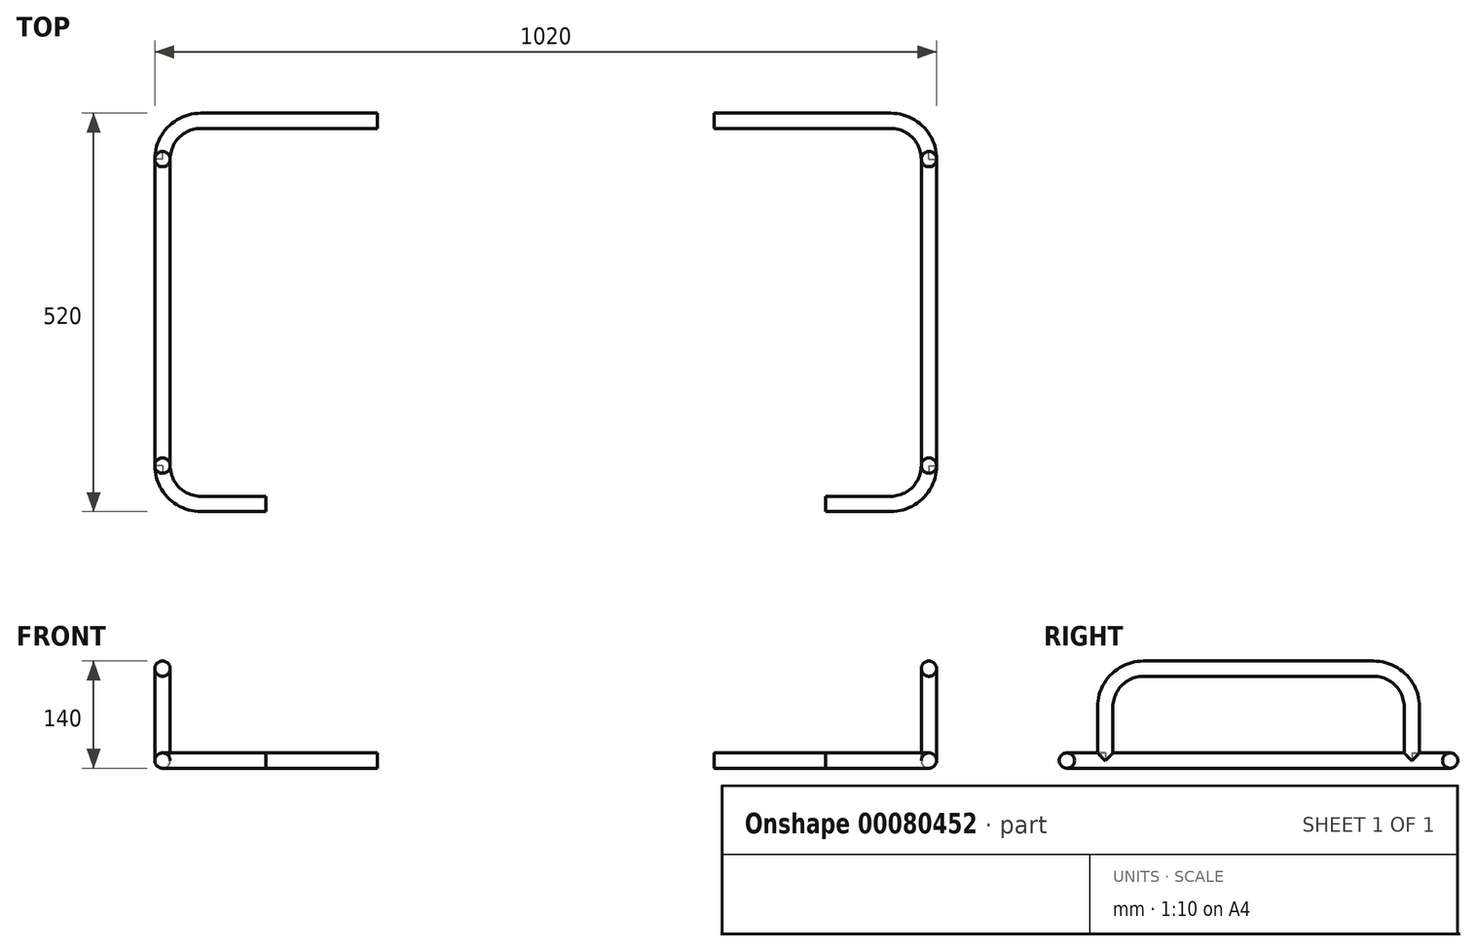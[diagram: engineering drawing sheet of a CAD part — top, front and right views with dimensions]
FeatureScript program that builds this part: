
annotation { "Feature Type Name" : "Feature", "Feature Type Description" : "" }
export const myFeature = defineFeature(function(context is Context, id is Id, definition is map)
    precondition{}
    {
        {
            var Q0;
            Q0=qCreatedBy(makeId("Top.planeOp"),FACE);
            var sketch = newSketch(context, id + "F0", { "sketchPlane" : qUnion([Q0])});
            skLineSegment(sketch, "E0", {"start": v(0, 0) * mm, "end": v(55, 0) * mm});
            skLineSegment(sketch, "E1", {"start": v(105, 50) * mm, "end": v(105, 450) * mm});
            skLineSegment(sketch, "E2", {"start": v(55, 500) * mm, "end": v(-145, 500) * mm});
            skLineSegment(sketch, "E3", {"start": v(-395, 732.64) * mm, "end": v(-395, -307.47) * mm, "construction": true});
            skPoint(sketch, "E4.visualSharp", {"position": v(105, 0) * mm});
            skArc(sketch, "E4.filletArc", {"start": v(55, 0) * mm, "mid": v(90.36, 14.64) * mm, "end": v(105, 50) * mm});
            skPoint(sketch, "E5.visualSharp", {"position": v(105, 500) * mm});
            skArc(sketch, "E5.filletArc", {"start": v(105, 450) * mm, "mid": v(90.36, 485.36) * mm, "end": v(55, 500) * mm});
            skSolve(sketch);
        }
        {
            var Q0;
            Q0=qCreatedBy(makeId("Right.planeOp"),FACE);
            var sketch = newSketch(context, id + "F1", { "sketchPlane" : qUnion([Q0])});
            skCircle(sketch, "E6", {"center": v(0, 0) * mm, "radius": 10 * mm});
            skSolve(sketch);
        }
        {
            var Q0;
            Q0=makeQuery(id+"F1.imprint","IMPRINT",FACE,{"disambiguationData":[TD([[makeQuery(id+"F1.imprint","IMPRINT",EDGE,{"derivedFrom":sQuery(id+"F1.wireOp",EDGE,"E6")}),1.0]])]});
            var Q1;
            Q1=sQuery(id+"F0.wireOp",EDGE,"E0");
            var Q2;
            Q2=sQuery(id+"F0.wireOp",EDGE,"E4.filletArc");
            var Q3;
            Q3=sQuery(id+"F0.wireOp",EDGE,"E1");
            var Q4;
            Q4=sQuery(id+"F0.wireOp",EDGE,"E5.filletArc");
            var Q5;
            Q5=sQuery(id+"F0.wireOp",EDGE,"E2");
            sweep(context, id + "F2", {"profiles" : qUnion([Q0]), "path" : qUnion([Q1, Q2, Q3, Q4, Q5])});
        }
        {
            var Q0;
            Q0=makeQuery(id+"F2.opSweep","CAP_FACE",FACE,{"disambiguationData":[OSD([sQuery(id+"F0.wireOp",VERTEX,"E0.start"),sQuery(id+"F1.wireOp",EDGE,"E6")])],"isStart":true});
            var Q1;
            Q1=makeQuery(id+"F2.opSweep","CAP_FACE",FACE,{"disambiguationData":[OSD([sQuery(id+"F0.wireOp",VERTEX,"E2.end"),sQuery(id+"F1.wireOp",EDGE,"E6")])],"isStart":false});
            extrude(context, id + "F3", {"entities" : qUnion([Q0, Q1]), "operationType" : NewBodyOperationType.ADD, "depth" : 30 * mm});
        }
        {
            var Q0;
            Q0=qCreatedBy(makeId("Right.planeOp"),FACE);
            var Q1;
            Q1=sQuery(id+"F0.wireOp",VERTEX,"E4.filletArc.end");
            cPlane(context, id + "F4", {"entities" : qUnion([Q0, Q1]), "cplaneType" : CPlaneType.PLANE_POINT, "offset" : 150 * mm, "width" : 150 * mm, "height" : 150 * mm});
        }
        {
            var Q0;
            Q0=qCreatedBy(id+"F4.planeOp",FACE);
            var sketch = newSketch(context, id + "F5", { "sketchPlane" : qUnion([Q0])});
            skPoint(sketch, "E7.0", {"position": v(50, 0) * mm});
            skPoint(sketch, "E7.1", {"position": v(450, 0) * mm});
            skLineSegment(sketch, "E8", {"start": v(50, 0) * mm, "end": v(50, 70) * mm});
            skLineSegment(sketch, "E9", {"start": v(100, 120) * mm, "end": v(400, 120) * mm});
            skLineSegment(sketch, "E10", {"start": v(450, 70) * mm, "end": v(450, 0) * mm});
            skPoint(sketch, "E11.visualSharp", {"position": v(50, 120) * mm});
            skArc(sketch, "E11.filletArc", {"start": v(100, 120) * mm, "mid": v(64.64, 105.36) * mm, "end": v(50, 70) * mm});
            skPoint(sketch, "E12.visualSharp", {"position": v(450, 120) * mm});
            skArc(sketch, "E12.filletArc", {"start": v(450, 70) * mm, "mid": v(435.36, 105.36) * mm, "end": v(400, 120) * mm});
            skSolve(sketch);
        }
        {
            var Q0;
            Q0=sQuery(id+"F5.wireOp",VERTEX,"E8.end");
            var Q1;
            Q1=sQuery(id+"F5.wireOp",EDGE,"E8");
            cPlane(context, id + "F6", {"entities" : qUnion([Q0, Q1]), "cplaneType" : CPlaneType.LINE_POINT, "offset" : 150 * mm, "width" : 150 * mm, "height" : 150 * mm});
        }
        {
            var Q0;
            Q0=qCreatedBy(id+"F6.planeOp",FACE);
            var sketch = newSketch(context, id + "F7", { "sketchPlane" : qUnion([Q0])});
            skPoint(sketch, "E13.0", {"position": v(105, 50) * mm});
            skCircle(sketch, "E14", {"center": v(105, 50) * mm, "radius": 10 * mm});
            skSolve(sketch);
        }
        {
            var Q0;
            Q0=makeQuery(id+"F7.imprint","IMPRINT",FACE,{"disambiguationData":[TD([[makeQuery(id+"F7.imprint","IMPRINT",EDGE,{"derivedFrom":sQuery(id+"F7.wireOp",EDGE,"E14")}),1.0]])]});
            var Q1;
            Q1=sQuery(id+"F5.wireOp",EDGE,"E11.filletArc");
            var Q2;
            Q2=sQuery(id+"F5.wireOp",EDGE,"E9");
            var Q3;
            Q3=sQuery(id+"F5.wireOp",EDGE,"E12.filletArc");
            sweep(context, id + "F8", {"profiles" : qUnion([Q0]), "path" : qUnion([Q1, Q2, Q3])});
        }
        {
            var Q0;
            Q0=makeQuery(id+"F8.opSweep","CAP_FACE",FACE,{"disambiguationData":[OSD([sQuery(id+"F5.wireOp",VERTEX,"E11.filletArc.end"),sQuery(id+"F7.wireOp",EDGE,"E14")])],"isStart":true});
            var Q1;
            Q1=makeQuery(id+"F8.opSweep","CAP_FACE",FACE,{"disambiguationData":[OSD([sQuery(id+"F5.wireOp",VERTEX,"E12.filletArc.start"),sQuery(id+"F7.wireOp",EDGE,"E14")])],"isStart":false});
            var Q2;
            Q2=makeQuery(id+"F2.opSweep","SWEPT_FACE",FACE,{"disambiguationData":[OSD([sQuery(id+"F0.wireOp",EDGE,"E1"),sQuery(id+"F1.wireOp",EDGE,"E6")])]});
            extrude(context, id + "F9", {"entities" : qUnion([Q0, Q1]), "operationType" : NewBodyOperationType.ADD, "endBound" : BoundingType.UP_TO_SURFACE, "endBoundEntityFace" : qUnion([Q2]), "depth" : 25 * mm});
        }
        {
            var Q0;
            Q0=qCreatedBy(makeId("Right.planeOp"),FACE);
            var Q1;
            Q1=sQuery(id+"F0.wireOp",VERTEX,"E3.end");
            cPlane(context, id + "F10", {"entities" : qUnion([Q0, Q1]), "cplaneType" : CPlaneType.PLANE_POINT, "offset" : 150 * mm, "width" : 150 * mm, "height" : 150 * mm});
        }
        {
            var Q0;
            Q0=makeQuery(id+"F2.opSweep","SWEPT_BODY",BODY,{"disambiguationData":[OSD([sQuery(id+"F0.wireOp",EDGE,"E2"),sQuery(id+"F1.wireOp",EDGE,"E6")])]});
            var Q1;
            Q1=makeQuery(id+"F8.opSweep","SWEPT_BODY",BODY,{"disambiguationData":[OSD([sQuery(id+"F5.wireOp",EDGE,"E12.filletArc"),sQuery(id+"F7.wireOp",EDGE,"E14")])]});
            var Q2;
            Q2=qCreatedBy(id+"F10.planeOp",FACE);
            mirror(context, id + "F11", {"entities" : qUnion([Q0, Q1]), "mirrorPlane" : qUnion([Q2])});
        }
    });
